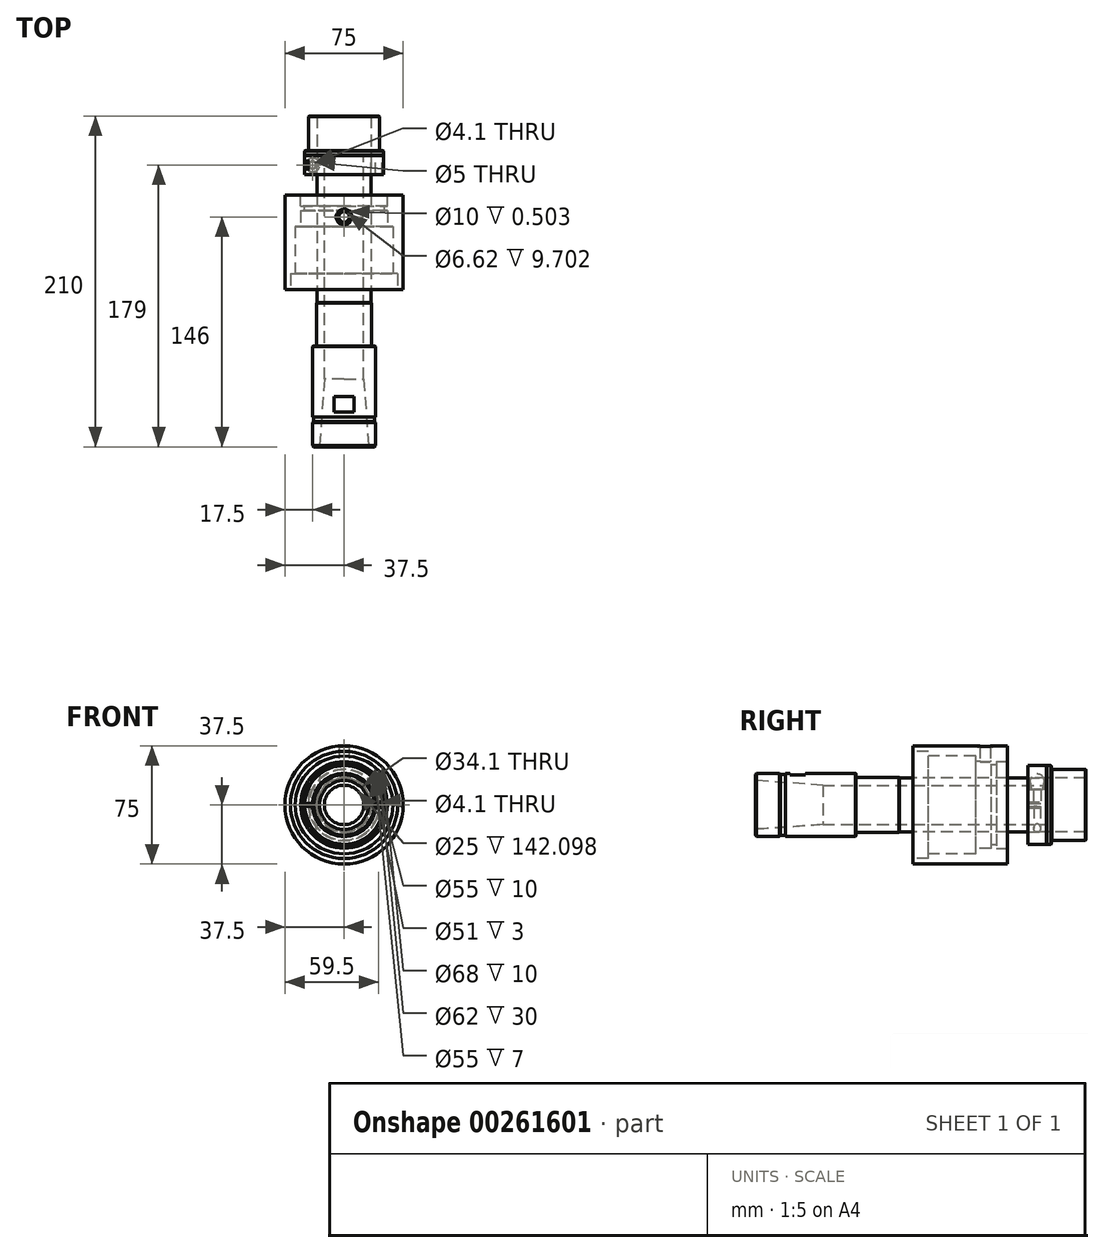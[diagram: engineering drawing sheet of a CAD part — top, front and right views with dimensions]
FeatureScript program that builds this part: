
annotation { "Feature Type Name" : "Feature", "Feature Type Description" : "" }
export const myFeature = defineFeature(function(context is Context, id is Id, definition is map)
    precondition{}
    {
        {
            var Q0;
            Q0=qCreatedBy(makeId("Front.planeOp"),FACE);
            var sketch = newSketch(context, id + "F0", { "sketchPlane" : qUnion([Q0])});
            skCircle(sketch, "E0", {"center": v(0, 0) * mm, "radius": 37.5 * mm});
            skCircle(sketch, "E1", {"center": v(0, 0) * mm, "radius": 25.5 * mm});
            skSolve(sketch);
        }
        {
            var Q0;
            Q0=qSketchRegion(id+"F0",true);
            extrude(context, id + "F1", {"entities" : qUnion([Q0]), "oppositeDirection" : true, "depth" : 60 * mm});
        }
        {
            var Q0;
            Q0=makeQuery(id+"F1.opExtrude","CAP_FACE",FACE,{"disambiguationData":[OSD([sQuery(id+"F0.wireOp",EDGE,"E0"),sQuery(id+"F0.wireOp",EDGE,"E1")])],"isStart":true});
            var sketch = newSketch(context, id + "F2", { "sketchPlane" : qUnion([Q0])});
            skCircle(sketch, "E2", {"center": v(0, 0) * mm, "radius": 34 * mm});
            skSolve(sketch);
        }
        {
            var Q0;
            Q0=qSketchRegion(id+"F2",true);
            extrude(context, id + "F3", {"entities" : qUnion([Q0]), "operationType" : NewBodyOperationType.REMOVE, "oppositeDirection" : true, "depth" : 10 * mm});
        }
        {
            var Q0;
            Q0=makeQuery(id+"F3.boolean.opBoolean","COPY",FACE,{"derivedFrom":makeQuery(id+"F3.opExtrude","CAP_FACE",FACE,{"disambiguationData":[OSD([sQuery(id+"F2.wireOp",EDGE,"E2")])],"isStart":false})});
            var sketch = newSketch(context, id + "F4", { "sketchPlane" : qUnion([Q0])});
            skCircle(sketch, "E3", {"center": v(0, 0) * mm, "radius": 31 * mm});
            skSolve(sketch);
        }
        {
            var Q0;
            Q0=qSketchRegion(id+"F4",true);
            extrude(context, id + "F5", {"entities" : qUnion([Q0]), "operationType" : NewBodyOperationType.REMOVE, "oppositeDirection" : true, "depth" : 30 * mm});
        }
        {
            var Q0;
            Q0=makeQuery(id+"F5.boolean.opBoolean","COPY",FACE,{"derivedFrom":makeQuery(id+"F5.opExtrude","CAP_FACE",FACE,{"disambiguationData":[OSD([sQuery(id+"F4.wireOp",EDGE,"E3")])],"isStart":false})});
            var sketch = newSketch(context, id + "F6", { "sketchPlane" : qUnion([Q0])});
            skCircle(sketch, "E4", {"center": v(0, 0) * mm, "radius": 27.5 * mm});
            skSolve(sketch);
        }
        {
            var Q0;
            Q0=qSketchRegion(id+"F6",true);
            extrude(context, id + "F7", {"entities" : qUnion([Q0]), "operationType" : NewBodyOperationType.REMOVE, "oppositeDirection" : true, "depth" : 10 * mm});
        }
        {
            var Q0;
            Q0=makeQuery(id+"F1.opExtrude","CAP_FACE",FACE,{"disambiguationData":[OSD([sQuery(id+"F0.wireOp",EDGE,"E0"),sQuery(id+"F0.wireOp",EDGE,"E1")])],"isStart":false});
            var sketch = newSketch(context, id + "F8", { "sketchPlane" : qUnion([Q0])});
            skCircle(sketch, "E5", {"center": v(0, 0) * mm, "radius": 27.5 * mm});
            skSolve(sketch);
        }
        {
            var Q0;
            Q0=qSketchRegion(id+"F8",true);
            extrude(context, id + "F9", {"entities" : qUnion([Q0]), "operationType" : NewBodyOperationType.REMOVE, "oppositeDirection" : true, "depth" : 7 * mm});
        }
        {
            var Q0;
            Q0=qCreatedBy(makeId("Top.planeOp"),FACE);
            cPlane(context, id + "F10", {"entities" : qUnion([Q0]), "cplaneType" : CPlaneType.OFFSET, "offset" : (75 / 2) * mm, "width" : 150 * mm, "height" : 150 * mm});
        }
        {
            var Q0;
            Q0=qCreatedBy(id+"F10.planeOp",FACE);
            var sketch = newSketch(context, id + "F11", { "sketchPlane" : qUnion([Q0])});
            skLineSegment(sketch, "E6", {"start": v(0, 0) * mm, "end": v(0, 60) * mm, "construction": true});
            skPoint(sketch, "E7", {"position": v(0, 46) * mm});
            skCircle(sketch, "E8", {"center": v(0, 46) * mm, "radius": 5 * mm});
            skSolve(sketch);
        }
        {
            var Q0;
            Q0=qSketchRegion(id+"F11",true);
            extrude(context, id + "F12", {"entities" : qUnion([Q0]), "operationType" : NewBodyOperationType.REMOVE, "flatOperationType" : FlatOperationType.REMOVE, "oppositeDirection" : true, "offsetDistance" : 25 * mm, "depth" : .5 * mm, "domain" : OperationDomain.MODEL});
        }
        {
            var Q0;
            Q0=makeQuery(id+"F12.boolean.opBoolean","COPY",FACE,{"derivedFrom":makeQuery(id+"F12.opExtrude","CAP_FACE",FACE,{"disambiguationData":[OSD([sQuery(id+"F11.wireOp",EDGE,"E8")])],"isStart":false})});
            var sketch = newSketch(context, id + "F13", { "sketchPlane" : qUnion([Q0])});
            skPoint(sketch, "E9", {"position": v(0, 46) * mm});
            skSolve(sketch);
        }
        {
            var Q0;
            Q0=sQuery(id+"F13.wireOp",VERTEX,"E9");
            var Q1;
            Q1=makeQuery(id+"F1.opExtrude","SWEPT_BODY",BODY,{"disambiguationData":[OSD([sQuery(id+"F0.wireOp",EDGE,"E0"),sQuery(id+"F0.wireOp",EDGE,"E1")])]});
            hole(context, id + "F14", {"style" : HoleStyle.SIMPLE, "endStyle" : HoleEndStyle.BLIND, "holeDiameter" : 6.62 * mm, "holeDepth" : 12 * mm, "locations" : qUnion([Q0]), "scope" : qUnion([Q1]), "startStyle" : HoleStartStyle.PART});
        }
        {
            var Q0;
            Q0=qCreatedBy(makeId("Front.planeOp"),FACE);
            cPlane(context, id + "F15", {"entities" : qUnion([Q0]), "cplaneType" : CPlaneType.OFFSET, "offset" : 100 * mm, "width" : 150 * mm, "height" : 150 * mm});
        }
        {
            var Q0;
            Q0=qCreatedBy(id+"F15.planeOp",FACE);
            var sketch = newSketch(context, id + "F16", { "sketchPlane" : qUnion([Q0])});
            skCircle(sketch, "E10", {"center": v(0, 0) * mm, "radius": 20 * mm});
            skSolve(sketch);
        }
        {
            var Q0;
            Q0=qSketchRegion(id+"F16",true);
            extrude(context, id + "F17", {"entities" : qUnion([Q0]), "oppositeDirection" : true, "depth" : 16 * mm});
        }
        {
            var Q0;
            Q0=makeQuery(id+"F17.opExtrude","CAP_FACE",FACE,{"disambiguationData":[OSD([sQuery(id+"F16.wireOp",EDGE,"E10")])],"isStart":false});
            var sketch = newSketch(context, id + "F18", { "sketchPlane" : qUnion([Q0])});
            skCircle(sketch, "E11", {"center": v(0, 0) * mm, "radius": 19.25 * mm});
            skSolve(sketch);
        }
        {
            var Q0;
            Q0=qSketchRegion(id+"F18",true);
            extrude(context, id + "F19", {"entities" : qUnion([Q0]), "operationType" : NewBodyOperationType.ADD, "depth" : 3 * mm});
        }
        {
            var Q0;
            Q0=makeQuery(id+"F19.opExtrude","CAP_FACE",FACE,{"disambiguationData":[OSD([sQuery(id+"F18.wireOp",EDGE,"E11")])],"isStart":false});
            var sketch = newSketch(context, id + "F20", { "sketchPlane" : qUnion([Q0])});
            skCircle(sketch, "E12", {"center": v(0, 0) * mm, "radius": 20 * mm});
            skSolve(sketch);
        }
        {
            var Q0;
            Q0=qSketchRegion(id+"F20",true);
            extrude(context, id + "F21", {"entities" : qUnion([Q0]), "operationType" : NewBodyOperationType.ADD, "depth" : 45 * mm});
        }
        {
            var Q0;
            Q0=makeQuery(id+"F21.opExtrude","CAP_FACE",FACE,{"disambiguationData":[OSD([sQuery(id+"F20.wireOp",EDGE,"E12")])],"isStart":false});
            var sketch = newSketch(context, id + "F22", { "sketchPlane" : qUnion([Q0])});
            skCircle(sketch, "E13", {"center": v(0, 0) * mm, "radius": 17.5 * mm});
            skSolve(sketch);
        }
        {
            var Q0;
            Q0=qSketchRegion(id+"F22",true);
            extrude(context, id + "F23", {"entities" : qUnion([Q0]), "operationType" : NewBodyOperationType.ADD, "depth" : 27.5 * mm});
        }
        {
            var Q0;
            Q0=makeQuery(id+"F23.opExtrude","CAP_FACE",FACE,{"disambiguationData":[OSD([sQuery(id+"F22.wireOp",EDGE,"E13")])],"isStart":false});
            var sketch = newSketch(context, id + "F24", { "sketchPlane" : qUnion([Q0])});
            skCircle(sketch, "E14", {"center": v(0, 0) * mm, "radius": 17 * mm});
            skSolve(sketch);
        }
        {
            var Q0;
            Q0=qSketchRegion(id+"F24",true);
            extrude(context, id + "F25", {"entities" : qUnion([Q0]), "operationType" : NewBodyOperationType.ADD, "depth" : 140 * mm});
        }
        {
            var Q0;
            Q0=makeQuery(id+"F25.opExtrude","CAP_FACE",FACE,{"disambiguationData":[OSD([sQuery(id+"F24.wireOp",EDGE,"E14")])],"isStart":false});
            var sketch = newSketch(context, id + "F26", { "sketchPlane" : qUnion([Q0])});
            skCircle(sketch, "E15", {"center": v(0, 0) * mm, "radius": 15.88 * mm});
            skSolve(sketch);
        }
        {
            var Q0;
            Q0=qSketchRegion(id+"F26",true);
            extrude(context, id + "F27", {"entities" : qUnion([Q0]), "operationType" : NewBodyOperationType.ADD, "depth" : 50 * mm});
        }
        {
            var Q0;
            Q0=makeQuery(id+"F17.opExtrude","CAP_FACE",FACE,{"disambiguationData":[OSD([sQuery(id+"F16.wireOp",EDGE,"E10")])],"isStart":true});
            var sketch = newSketch(context, id + "F28", { "sketchPlane" : qUnion([Q0])});
            skCircle(sketch, "E16", {"center": v(0, 0) * mm, "radius": 15.5 * mm});
            skSolve(sketch);
        }
        {
            var Q0;
            Q0=qSketchRegion(id+"F28",true);
            extrude(context, id + "F29", {"entities" : qUnion([Q0]), "operationType" : NewBodyOperationType.REMOVE, "oppositeDirection" : true, "depth" : 50 * mm, "hasDraft" : true, "draftAngle" : 4 * degree, "draftPullDirection" : true});
        }
        {
            var Q0;
            Q0=makeQuery(id+"F27.opExtrude","CAP_FACE",FACE,{"disambiguationData":[OSD([sQuery(id+"F26.wireOp",EDGE,"E15")])],"isStart":false});
            var sketch = newSketch(context, id + "F30", { "sketchPlane" : qUnion([Q0])});
            skCircle(sketch, "E17", {"center": v(0, 0) * mm, "radius": 12.5 * mm});
            skSolve(sketch);
        }
        {
            var Q0;
            Q0=qSketchRegion(id+"F30",true);
            extrude(context, id + "F31", {"entities" : qUnion([Q0]), "operationType" : NewBodyOperationType.REMOVE, "endBound" : BoundingType.THROUGH_ALL, "oppositeDirection" : true, "depth" : 25 * mm});
        }
        {
            var Q0;
            Q0=makeQuery(id+"F1.opExtrude","CAP_FACE",FACE,{"disambiguationData":[OSD([sQuery(id+"F0.wireOp",EDGE,"E0"),sQuery(id+"F0.wireOp",EDGE,"E1")])],"isStart":false});
            cPlane(context, id + "F32", {"entities" : qUnion([Q0]), "cplaneType" : CPlaneType.OFFSET, "offset" : 25 * mm, "width" : 150 * mm, "height" : 150 * mm});
        }
        {
            var Q0;
            Q0=qCreatedBy(id+"F32.planeOp",FACE);
            var sketch = newSketch(context, id + "F33", { "sketchPlane" : qUnion([Q0])});
            skCircle(sketch, "E18", {"center": v(0, 0) * mm, "radius": 25 * mm});
            skSolve(sketch);
        }
        {
            var Q0;
            Q0=qSketchRegion(id+"F33",true);
            extrude(context, id + "F34", {"entities" : qUnion([Q0]), "depth" : 3 * mm});
        }
        {
            var Q0;
            Q0=makeQuery(id+"F34.opExtrude","CAP_FACE",FACE,{"disambiguationData":[OSD([sQuery(id+"F33.wireOp",EDGE,"E18")])],"isStart":false});
            var sketch = newSketch(context, id + "F35", { "sketchPlane" : qUnion([Q0])});
            skCircle(sketch, "E19", {"center": v(0, 0) * mm, "radius": 22.5 * mm});
            skSolve(sketch);
        }
        {
            var Q0;
            Q0=qSketchRegion(id+"F35",true);
            extrude(context, id + "F36", {"entities" : qUnion([Q0]), "operationType" : NewBodyOperationType.ADD, "depth" : 22 * mm});
        }
        {
            var Q0;
            Q0=makeQuery(id+"F34.opExtrude","CAP_FACE",FACE,{"disambiguationData":[OSD([sQuery(id+"F33.wireOp",EDGE,"E18")])],"isStart":true});
            var sketch = newSketch(context, id + "F37", { "sketchPlane" : qUnion([Q0])});
            skCircle(sketch, "E20", {"center": v(0, 0) * mm, "radius": 17.05 * mm});
            skSolve(sketch);
        }
        {
            var Q0;
            Q0=qSketchRegion(id+"F37",true);
            extrude(context, id + "F38", {"entities" : qUnion([Q0]), "operationType" : NewBodyOperationType.REMOVE, "endBound" : BoundingType.UP_TO_NEXT, "oppositeDirection" : true, "depth" : 25 * mm});
        }
        {
            var Q0;
            Q0=makeQuery(id+"F34.opExtrude","SWEPT_FACE",FACE,{"disambiguationData":[OSD([sQuery(id+"F33.wireOp",EDGE,"E18")])]});
            var Q1;
            Q1=makeQuery(id+"F36.opExtrude","SWEPT_FACE",FACE,{"disambiguationData":[OSD([sQuery(id+"F35.wireOp",EDGE,"E19")])]});
            var Q2;
            Q2=makeQuery(id+"F38.boolean.opBoolean","COPY",FACE,{"derivedFrom":makeQuery(id+"F38.opExtrude","SWEPT_FACE",FACE,{"disambiguationData":[OSD([sQuery(id+"F37.wireOp",EDGE,"E20")])]})});
            chamfer(context, id + "F39", {"entities" : qUnion([Q0, Q1, Q2]), "width" : .25 * mm, "tangentPropagation" : true});
        }
        {
            var Q0;
            Q0=makeQuery(id+"F17.opExtrude","SWEPT_FACE",FACE,{"disambiguationData":[OSD([sQuery(id+"F16.wireOp",EDGE,"E10")])]});
            var Q1;
            Q1=makeQuery(id+"FgnukjYGfaEQPH9_2.opExtrude","SWEPT_FACE",FACE,{"disambiguationData":[OSD([sQuery(id+"Fpo6LL3ajyrS8uz_2.wireOp",EDGE,"ZPJ78Gsf-ZMfG-ODoI-Mz2S-bczQQD3Yarib")])]});
            var Q2;
            Q2=makeQuery(id+"FODl2dEUZz75cc0_5.opExtrude","CAP_FACE",FACE,{"disambiguationData":[OSD([sQuery(id+"F1eT8sYVKhEZkZg_5.wireOp",EDGE,"IbQkoDR8-f8DR-9itt-bgPZ-ocWSv4ODY6js")])],"isStart":false});
            chamfer(context, id + "F40", {"entities" : qUnion([Q0, Q1, Q2]), "width" : .75 * mm, "tangentPropagation" : true});
        }
        {
            var Q0;
            Q0=qCreatedBy(makeId("Right.planeOp"),FACE);
            var sketch = newSketch(context, id + "F41", { "sketchPlane" : qUnion([Q0])});
            skLineSegment(sketch, "E21.bottom", {"start": v(-68, 21) * mm, "end": v(-78, 21) * mm});
            skLineSegment(sketch, "E21.top", {"start": v(-68, 19) * mm, "end": v(-78, 19) * mm});
            skLineSegment(sketch, "E21.left", {"start": v(-68, 21) * mm, "end": v(-68, 19) * mm});
            skLineSegment(sketch, "E21.right", {"start": v(-78, 21) * mm, "end": v(-78, 19) * mm});
            skPoint(sketch, "E21.middle", {"position": v(-73, 20) * mm});
            skSolve(sketch);
        }
        {
            var Q0;
            Q0=qSketchRegion(id+"F41",true);
            extrude(context, id + "F42", {"entities" : qUnion([Q0]), "operationType" : NewBodyOperationType.REMOVE, "depth" : 15 * mm, "symmetric" : true});
        }
        {
            var Q0;
            Q0=makeQuery(id+"F23.opExtrude","CAP_EDGE",EDGE,{"disambiguationData":[OSD([sQuery(id+"F22.wireOp",EDGE,"E13")])],"isStart":false});
            var Q1;
            Q1=makeQuery(id+"F21.opExtrude","CAP_EDGE",EDGE,{"disambiguationData":[OSD([sQuery(id+"F20.wireOp",EDGE,"E12")])],"isStart":false});
            var Q2;
            Q2=makeQuery(id+"F25.opExtrude","CAP_EDGE",EDGE,{"disambiguationData":[OSD([sQuery(id+"F24.wireOp",EDGE,"E14")])],"isStart":false});
            var Q3;
            Q3=makeQuery(id+"F27.opExtrude","CAP_FACE",FACE,{"disambiguationData":[OSD([sQuery(id+"F26.wireOp",EDGE,"E15")])],"isStart":false});
            chamfer(context, id + "F43", {"entities" : qUnion([Q0, Q1, Q2, Q3]), "width" : .25 * mm, "tangentPropagation" : true});
        }
        {
            var Q0;
            Q0=makeQuery(id+"F34.opExtrude","CAP_FACE",FACE,{"disambiguationData":[OSD([sQuery(id+"F33.wireOp",EDGE,"E18")])],"isStart":true});
            var sketch = newSketch(context, id + "F44", { "sketchPlane" : qUnion([Q0])});
            skCircle(sketch, "E22", {"center": v(0, 0) * mm, "radius": 25 * mm});
            skCircle(sketch, "E23", {"center": v(0, 0) * mm, "radius": 17.05 * mm});
            skSolve(sketch);
        }
        {
            var Q0;
            Q0=qSketchRegion(id+"F44",true);
            extrude(context, id + "F45", {"entities" : qUnion([Q0]), "depth" : 12 * mm});
        }
        {
            var Q0;
            Q0=qCreatedBy(makeId("Top.planeOp"),FACE);
            cPlane(context, id + "F46", {"entities" : qUnion([Q0]), "cplaneType" : CPlaneType.OFFSET, "offset" : 10 * mm, "width" : 150 * mm, "height" : 150 * mm});
        }
        {
            var Q0;
            Q0=qCreatedBy(id+"F46.planeOp",FACE);
            var sketch = newSketch(context, id + "F47", { "sketchPlane" : qUnion([Q0])});
            skPoint(sketch, "E24", {"position": v(-20, 79) * mm});
            skCircle(sketch, "E25", {"center": v(-20, 79) * mm, "radius": 4.5 * mm});
            skSolve(sketch);
        }
        {
            var Q0;
            Q0=qSketchRegion(id+"F47",true);
            var Q1;
            Q1=makeQuery(id+"F45.opExtrude","SWEPT_FACE",FACE,{"disambiguationData":[OSD([sQuery(id+"F44.wireOp",EDGE,"E22")])]});
            extrude(context, id + "F48", {"entities" : qUnion([Q0]), "operationType" : NewBodyOperationType.REMOVE, "endBound" : BoundingType.UP_TO_SURFACE, "endBoundEntityFace" : qUnion([Q1]), "depth" : 25 * mm});
        }
        {
            var Q0;
            Q0=makeQuery(id+"F48.boolean.opBoolean","COPY",FACE,{"derivedFrom":makeQuery(id+"F48.opExtrude","CAP_FACE",FACE,{"disambiguationData":[OSD([sQuery(id+"F47.wireOp",EDGE,"E25")])],"isStart":true})});
            var sketch = newSketch(context, id + "F49", { "sketchPlane" : qUnion([Q0])});
            skPoint(sketch, "E26", {"position": v(-20, 79) * mm});
            skSolve(sketch);
        }
        {
            var Q0;
            Q0=sQuery(id+"F49.wireOp",VERTEX,"E26");
            var Q1;
            Q1=makeQuery(id+"F45.opExtrude","SWEPT_BODY",BODY,{"disambiguationData":[OSD([sQuery(id+"F44.wireOp",EDGE,"E22"),sQuery(id+"F44.wireOp",EDGE,"E23")])]});
            hole(context, id + "F50", {"style" : HoleStyle.SIMPLE, "endStyle" : HoleEndStyle.THROUGH, "standardTappedOrClearance" : lookupTablePath({ "standard" : "ISO", "engagement" : "75%", "pitch" : "0.9 mm", "size" : "M5", "type" : "Tapped" }), "standardBlindInLast" : lookupTablePath({ "standard" : "ISO", "engagement" : "75%", "pitch" : "0.9 mm", "size" : "M5", "type" : "Tapped" }), "holeDiameter" : 4.1 * mm, "locations" : qUnion([Q0]), "scope" : qUnion([Q1]), "isTappedThrough" : true, "showTappedDepth" : true, "startStyle" : HoleStartStyle.PART});
        }
        {
            var Q0;
            Q0=sQuery(id+"F49.wireOp",VERTEX,"E26");
            var Q1;
            Q1=makeQuery(id+"F45.opExtrude","SWEPT_BODY",BODY,{"disambiguationData":[OSD([sQuery(id+"F44.wireOp",EDGE,"E22"),sQuery(id+"F44.wireOp",EDGE,"E23")])]});
            hole(context, id + "F51", {"style" : HoleStyle.SIMPLE, "endStyle" : HoleEndStyle.BLIND, "standardTappedOrClearance" : lookupTablePath({ "standard" : "ISO", "size" : "5", "type" : "Drilled" }), "standardBlindInLast" : lookupTablePath({ "standard" : "ISO", "size" : "5", "type" : "Drilled" }), "holeDiameter" : 5 * mm, "holeDepth" : 9 * mm, "locations" : qUnion([Q0]), "scope" : qUnion([Q1]), "startStyle" : HoleStartStyle.PART});
        }
        {
            var Q0;
            Q0=makeQuery(id+"F45.opExtrude","CAP_FACE",FACE,{"disambiguationData":[OSD([sQuery(id+"F44.wireOp",EDGE,"E22"),sQuery(id+"F44.wireOp",EDGE,"E23")])],"isStart":false});
            var sketch = newSketch(context, id + "F52", { "sketchPlane" : qUnion([Q0])});
            skLineSegment(sketch, "E27", {"start": v(0, 0) * mm, "end": v(-25, 0) * mm, "construction": true});
            skLineSegment(sketch, "E28.bottom", {"start": v(-16.5, 1) * mm, "end": v(-25.5, 1) * mm});
            skLineSegment(sketch, "E28.top", {"start": v(-16.5, -1) * mm, "end": v(-25.5, -1) * mm});
            skLineSegment(sketch, "E28.left", {"start": v(-16.5, 1) * mm, "end": v(-16.5, -1) * mm});
            skLineSegment(sketch, "E28.right", {"start": v(-25.5, 1) * mm, "end": v(-25.5, -1) * mm});
            skPoint(sketch, "E28.middle", {"position": v(-21, 0) * mm});
            skSolve(sketch);
        }
        {
            var Q0;
            Q0=qSketchRegion(id+"F52",true);
            extrude(context, id + "F53", {"entities" : qUnion([Q0]), "operationType" : NewBodyOperationType.REMOVE, "oppositeDirection" : true, "depth" : 12 * mm});
        }
        {
            var Q0;
            Q0=makeQuery(id+"F45.opExtrude","CAP_FACE",FACE,{"disambiguationData":[OSD([sQuery(id+"F44.wireOp",EDGE,"E22"),sQuery(id+"F44.wireOp",EDGE,"E23")])],"isStart":false});
            var sketch = newSketch(context, id + "F54", { "sketchPlane" : qUnion([Q0])});
            skLineSegment(sketch, "E29", {"start": v(0, 0) * mm, "end": v(25, 0) * mm, "construction": true});
            skPoint(sketch, "E30", {"position": v(0, 0) * mm});
            skPoint(sketch, "E31", {"position": v(22, 0) * mm});
            skSolve(sketch);
        }
        {
            var Q0;
            Q0=sQuery(id+"F54.wireOp",VERTEX,"E31");
            var Q1;
            Q1=makeQuery(id+"F45.opExtrude","SWEPT_BODY",BODY,{"disambiguationData":[OSD([sQuery(id+"F44.wireOp",EDGE,"E22"),sQuery(id+"F44.wireOp",EDGE,"E23")])]});
            hole(context, id + "F55", {"style" : HoleStyle.SIMPLE, "endStyle" : HoleEndStyle.THROUGH, "standardTappedOrClearance" : lookupTablePath({ "standard" : "ISO", "engagement" : "75%", "pitch" : "0.9 mm", "size" : "M5", "type" : "Tapped" }), "standardBlindInLast" : lookupTablePath({ "standard" : "ISO", "engagement" : "75%", "pitch" : "0.9 mm", "size" : "M5", "type" : "Tapped" }), "holeDiameter" : 4.1 * mm, "locations" : qUnion([Q0]), "scope" : qUnion([Q1]), "isTappedThrough" : true, "showTappedDepth" : true, "startStyle" : HoleStartStyle.PART});
        }
    });
